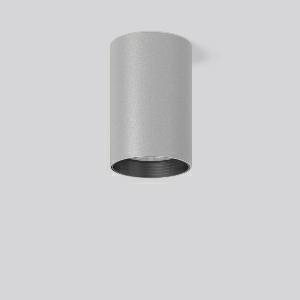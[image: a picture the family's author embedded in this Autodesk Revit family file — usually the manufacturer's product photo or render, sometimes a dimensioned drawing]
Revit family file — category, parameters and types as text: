
# Revit family: heledon_maxi_a_931227_004_2_76_a747
name_source: partatom
category: Lighting Fixtures
units: mm (PartAtom-declared; Revit-internal decimal feet)

## family parameters
Cut with Voids When Loaded = No
Host = Face
Light Source = No
Part Type = Normal
Room Calculation Point = No
Round Connector Dimension = Use Diameter
Shared = No

## types (1)
- HELEDON maxi A (1 x LED Modul 927, 3500 lm, 2700)
    Apparent Load = 35 VA
    Approval mark = CE
    CIE Flux Codes = 97 100 100 100 100
    Color Rendering = 92
    Color Temperature = 2700
    Default Elevation = 1800 mm
    Description = Series: HELEDON maxi
Cylindrical surface-mounted downlight. Housing: die-cast aluminium, powder-coated. Internal ceiling frame polycarbonate with bayonet mounting. Black plastic ring and recessed LED to prevent glare from the side. Optical assembly with lens made of plastic (polycarbonate) for the best homogeneous light distribution - can be changed without tools. Best colour rendering index Ra>90. Suitable for Ceiling mounting. Easy installation with a separate ceiling frame with bayonet mounting and plug connection. Driver integrated. Connected via plug-in connector. High quality converter without flickering and stroboscopic effect. The following accessories can be mounted without use of tools: interchangeable lenses, decorative glasses, honeycomb louvre, clear and frosted diffusers, white interchangeable plastic ring. 
Colour: silver
Diameter: 123 mm
Height: 183 mm
Lamp: LED
Socket: without socket
Colour temperature: 2700K
Colour rendering index (CRI): 92
System power: 35 W
Rated luminous flux: 3500 lm
Luminous efficiency: 100 lm/W
Control gear: Converter, dimmable, DALI
Protection class: I
Type of protection: IP 20
    Height = 183 mm
    Lamp = 1 x LED Modul 927
    Lamp Light Flux = 3500 lm
    Lamp count = 1
    Length = 123 mm
    Lifetime = 50000 h
    Luminous efficacy = 100 lm/W
    Manufacturer = RZB
    ModVariant = No
    Model = 931227.004.2.76
    Mounting Place = Ceiling
    Mounting Type = Surface mounted
    Number of Poles = 1
    OnlyDefault = Yes
    Power Factor = 1
    Product Name = HELEDON maxi A
    Product group = Surface mounted downlights
    ProductGroupID = 302
    Protection Class = Protection class I
    Protection Degree = IP 20
    RLX_Detail_Level = 1
    RLX_Emergency_Light_Flux = 0 lm
    RLX_Emergency_Type = 0
    RLX_Emergency_Type_DB = No
    RlxData = <blob elided: 97813 chars, md5=d9672d2e>
    Socket = socket
    Standby Power = 0 W
    System Light Flux = 3500 lm
    System Power = 35 W
    Type Comments = Product without accessories
    Type Image = 931193.004.jpg
    URL = http://relux.com
    VarID = ---
    Voltage = 230 V
    Voltage Range = 220-240 V
    Weight = 0.00 kg
    Width = 0 mm  [stored 0 ft]

note: [stored X ft] marks values corroborated as IEEE doubles in the binary element streams (Revit-internal decimal feet)

## geometry (parser evidence)
native form markers: Blend x4, Sweep x10
no freeform markers — native parametric forms only
